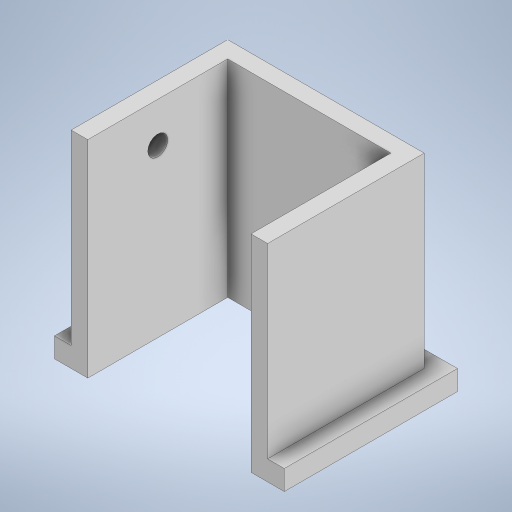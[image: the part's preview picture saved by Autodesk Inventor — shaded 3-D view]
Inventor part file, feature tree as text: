
AUTODESK INVENTOR PART (.ipt)
format: ipt  version: 2023 (Build 270158000, 158)  size: 264,704 bytes
history: native  units: in
note: dims shown in document units (in); Inventor stores cm internally (conversion verified against a paired STEP export)
features: sketch x5, extrude x4
ambient origin geometry x8: Origin, YZ Plane, XZ Plane, XY Plane, X Axis, Y Axis, Z Axis, Center Point
bodies: Solid1 (feature_tree)
feature tree (9):
  extrude  "Extrusion1"  Depth=0.1969in
  extrude  "Extrusion7"  Depth=1.6535in
  extrude  "Extrusion8"  Depth=1.6535in
  sketch  "Sketch9"  dims[d6=2.4409in d7=0.0in d34=0.1969in]
  extrude  "Extrusion9"  Depth=0.1969in
  sketch  "Sketch1"  dims[d0=2.3228in d1=0.1969in]
  sketch  "Sketch7"  dims[d2=0.1969in d3=1.6535in]
  sketch  "Sketch8"  dims[d4=0.1969in d5=1.6535in]
  sketch  "Sketch10"  dims[d35=2.0472in d36=0.1969in d37=2.0472in d38=0.2362in d39=0.0in d40=0.3937in d41=0.1969in d42=0.3937in d43=0.1969in d44=1.3583in d45=0.8268in d46=0.8268in d47=0.1969in d48=0.1969in d49=0.1969in d50=0.0in d51=0.8268in d52=1.9685in d53=0.2362in d54=0.1969in d55=0.0in d11=0.0197in d12=0.0344in d13=0.0197in d14=0.0344in]
